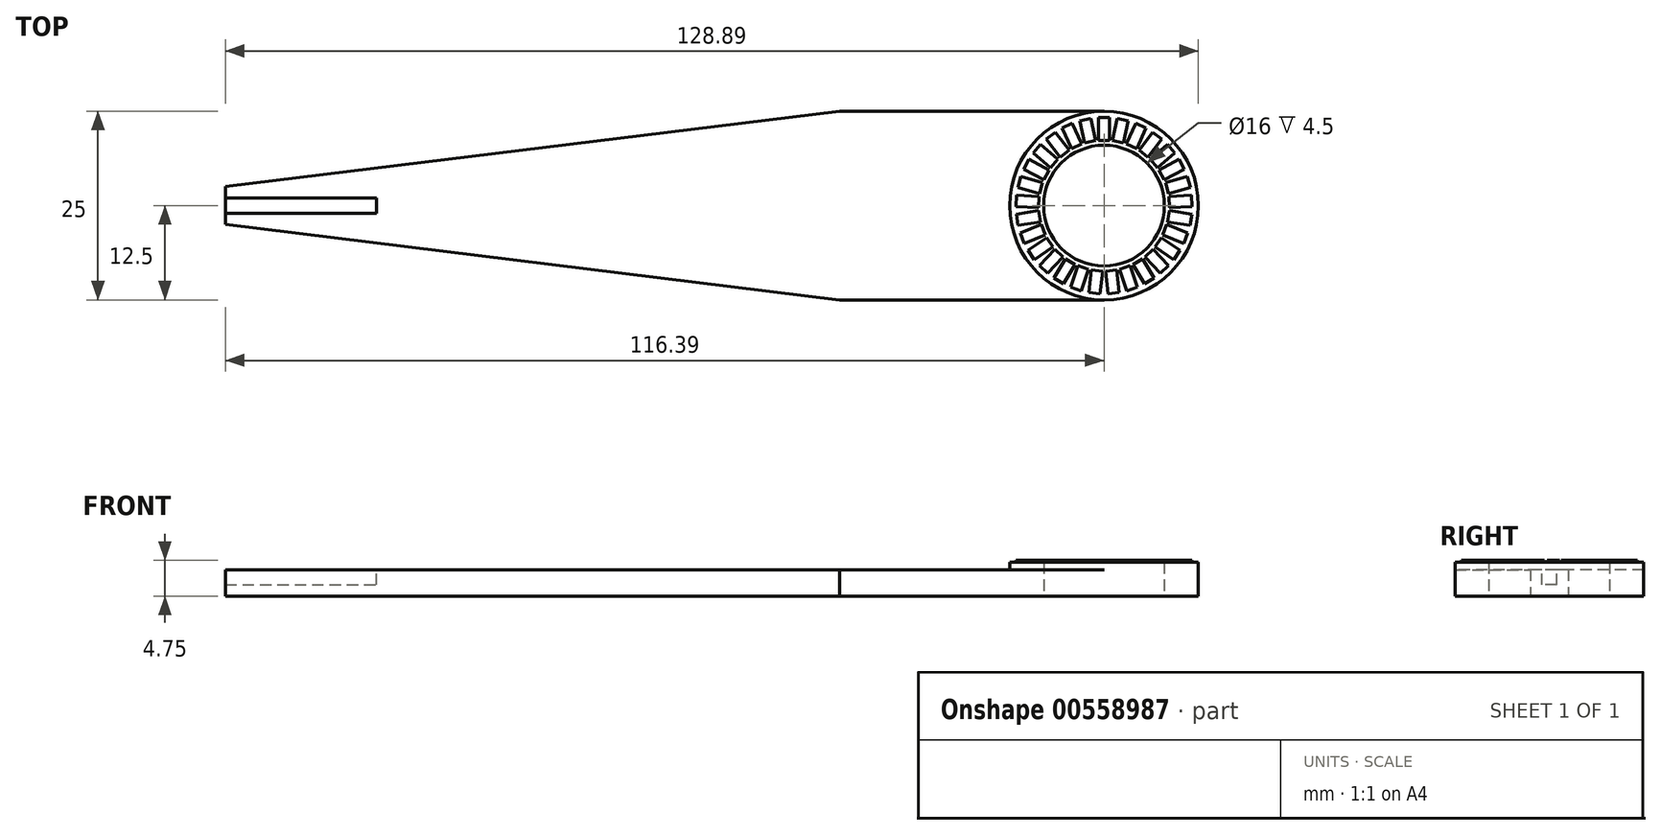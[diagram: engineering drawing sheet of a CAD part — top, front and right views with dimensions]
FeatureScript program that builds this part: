
annotation { "Feature Type Name" : "Feature", "Feature Type Description" : "" }
export const myFeature = defineFeature(function(context is Context, id is Id, definition is map)
    precondition{}
    {
        {
            var Q0;
            Q0=qCreatedBy(makeId("Top.planeOp"),FACE);
            var sketch = newSketch(context, id + "F0", { "sketchPlane" : qUnion([Q0])});
            skCircle(sketch, "E0", {"center": v(0, 0) * mm, "radius": 8 * mm});
            skCircle(sketch, "E1", {"center": v(0, 0) * mm, "radius": 12.5 * mm});
            skLineSegment(sketch, "E2", {"start": v(-35, 12.5) * mm, "end": v(0, 12.5) * mm});
            skLineSegment(sketch, "E3", {"start": v(-35, -12.5) * mm, "end": v(0, -12.5) * mm});
            skLineSegment(sketch, "E4", {"start": v(-35, 12.5) * mm, "end": v(-121.4, 12.5) * mm, "construction": true});
            skLineSegment(sketch, "E5", {"start": v(-35, 12.5) * mm, "end": v(-116.39, 2.5) * mm});
            skLineSegment(sketch, "E6", {"start": v(-35, -12.5) * mm, "end": v(-123.46, -12.5) * mm, "construction": true});
            skLineSegment(sketch, "E7", {"start": v(-35, -12.5) * mm, "end": v(-116.39, -2.5) * mm});
            skLineSegment(sketch, "E8", {"start": v(-116.39, 2.5) * mm, "end": v(-116.39, -2.5) * mm});
            skSolve(sketch);
        }
        {
            var Q0;
            Q0=qSketchRegion(id+"F0",true);
            extrude(context, id + "F1", {"entities" : qUnion([Q0]), "depth" : 3.5 * mm});
        }
        {
            var Q0;
            Q0=makeQuery(id+"F1.opExtrude","CAP_FACE",FACE,{"disambiguationData":[OSD([sQuery(id+"F0.wireOp",EDGE,"E0"),sQuery(id+"F0.wireOp",EDGE,"E1"),sQuery(id+"F0.wireOp",EDGE,"E2"),sQuery(id+"F0.wireOp",EDGE,"E3"),sQuery(id+"F0.wireOp",EDGE,"E5"),sQuery(id+"F0.wireOp",EDGE,"E7"),sQuery(id+"F0.wireOp",EDGE,"E8")])],"isStart":false});
            var sketch = newSketch(context, id + "F2", { "sketchPlane" : qUnion([Q0])});
            skCircle(sketch, "E9", {"center": v(0, 0) * mm, "radius": 12.5 * mm});
            skCircle(sketch, "E10", {"center": v(0, 0) * mm, "radius": 8 * mm});
            skSolve(sketch);
        }
        {
            var Q0;
            Q0=qSketchRegion(id+"F2",true);
            extrude(context, id + "F3", {"entities" : qUnion([Q0]), "operationType" : NewBodyOperationType.ADD, "depth" : 1 * mm});
        }
        {
            var Q0;
            Q0=makeQuery(id+"F1.opExtrude","CAP_FACE",FACE,{"disambiguationData":[OSD([sQuery(id+"F0.wireOp",EDGE,"E0"),sQuery(id+"F0.wireOp",EDGE,"E1"),sQuery(id+"F0.wireOp",EDGE,"E2"),sQuery(id+"F0.wireOp",EDGE,"E3"),sQuery(id+"F0.wireOp",EDGE,"E5"),sQuery(id+"F0.wireOp",EDGE,"E7"),sQuery(id+"F0.wireOp",EDGE,"E8")])],"isStart":false});
            var sketch = newSketch(context, id + "F4", { "sketchPlane" : qUnion([Q0])});
            skLineSegment(sketch, "E11.bottom", {"start": v(-116.39, 1) * mm, "end": v(-96.39, 1) * mm});
            skLineSegment(sketch, "E11.top", {"start": v(-116.39, -1) * mm, "end": v(-96.39, -1) * mm});
            skLineSegment(sketch, "E11.left", {"start": v(-116.39, 1) * mm, "end": v(-116.39, -1) * mm});
            skLineSegment(sketch, "E11.right", {"start": v(-96.39, 1) * mm, "end": v(-96.39, -1) * mm});
            skSolve(sketch);
        }
        {
            var Q0;
            Q0=qSketchRegion(id+"F4",true);
            extrude(context, id + "F5", {"entities" : qUnion([Q0]), "operationType" : NewBodyOperationType.REMOVE, "oppositeDirection" : true, "depth" : 2 * mm});
        }
        {
            var Q0;
            Q0=makeQuery(id+"F3.opExtrude","CAP_FACE",FACE,{"disambiguationData":[OSD([sQuery(id+"F2.wireOp",EDGE,"E9"),sQuery(id+"F2.wireOp",EDGE,"E10")])],"isStart":false});
            var sketch = newSketch(context, id + "F6", { "sketchPlane" : qUnion([Q0])});
            skLineSegment(sketch, "E12.bottom", {"start": v(-0.75, 11.65) * mm, "end": v(0.75, 11.65) * mm});
            skLineSegment(sketch, "E12.top", {"start": v(-0.75, 8.65) * mm, "end": v(0.75, 8.65) * mm});
            skLineSegment(sketch, "E12.left", {"start": v(-0.75, 11.65) * mm, "end": v(-0.75, 8.65) * mm});
            skLineSegment(sketch, "E12.right", {"start": v(0.75, 11.65) * mm, "end": v(0.75, 8.65) * mm});
            skLineSegment(sketch, "E13.1.0", {"start": v(1.77, 11.54) * mm, "end": v(1.13, 8.61) * mm});
            skLineSegment(sketch, "E13.1.1", {"start": v(1.13, 8.61) * mm, "end": v(2.6, 8.29) * mm});
            skLineSegment(sketch, "E13.1.2", {"start": v(1.77, 11.54) * mm, "end": v(3.24, 11.22) * mm});
            skLineSegment(sketch, "E13.1.3", {"start": v(3.24, 11.22) * mm, "end": v(2.6, 8.29) * mm});
            skLineSegment(sketch, "E13.2.0", {"start": v(4.21, 10.9) * mm, "end": v(2.95, 8.17) * mm});
            skLineSegment(sketch, "E13.2.1", {"start": v(2.95, 8.17) * mm, "end": v(4.31, 7.54) * mm});
            skLineSegment(sketch, "E13.2.2", {"start": v(4.21, 10.9) * mm, "end": v(5.57, 10.26) * mm});
            skLineSegment(sketch, "E13.2.3", {"start": v(5.57, 10.26) * mm, "end": v(4.31, 7.54) * mm});
            skLineSegment(sketch, "E13.3.0", {"start": v(6.46, 9.73) * mm, "end": v(4.64, 7.34) * mm});
            skLineSegment(sketch, "E13.3.1", {"start": v(4.64, 7.34) * mm, "end": v(5.83, 6.43) * mm});
            skLineSegment(sketch, "E13.3.2", {"start": v(6.46, 9.73) * mm, "end": v(7.65, 8.82) * mm});
            skLineSegment(sketch, "E13.3.3", {"start": v(7.65, 8.82) * mm, "end": v(5.83, 6.43) * mm});
            skLineSegment(sketch, "E13.4.0", {"start": v(8.4, 8.12) * mm, "end": v(6.1, 6.17) * mm});
            skLineSegment(sketch, "E13.4.1", {"start": v(6.1, 6.17) * mm, "end": v(7.08, 5.03) * mm});
            skLineSegment(sketch, "E13.4.2", {"start": v(8.4, 8.12) * mm, "end": v(9.37, 6.97) * mm});
            skLineSegment(sketch, "E13.4.3", {"start": v(9.37, 6.97) * mm, "end": v(7.08, 5.03) * mm});
            skLineSegment(sketch, "E13.5.0", {"start": v(9.94, 6.12) * mm, "end": v(7.3, 4.72) * mm});
            skLineSegment(sketch, "E13.5.1", {"start": v(7.3, 4.72) * mm, "end": v(8, 3.4) * mm});
            skLineSegment(sketch, "E13.5.2", {"start": v(9.94, 6.12) * mm, "end": v(10.65, 4.8) * mm});
            skLineSegment(sketch, "E13.5.3", {"start": v(10.65, 4.8) * mm, "end": v(8, 3.4) * mm});
            skLineSegment(sketch, "E13.6.0", {"start": v(11.03, 3.84) * mm, "end": v(8.14, 3.04) * mm});
            skLineSegment(sketch, "E13.6.1", {"start": v(8.14, 3.04) * mm, "end": v(8.54, 1.6) * mm});
            skLineSegment(sketch, "E13.6.2", {"start": v(11.03, 3.84) * mm, "end": v(11.43, 2.4) * mm});
            skLineSegment(sketch, "E13.6.3", {"start": v(11.43, 2.4) * mm, "end": v(8.54, 1.6) * mm});
            skLineSegment(sketch, "E13.7.0", {"start": v(11.6, 1.38) * mm, "end": v(8.6, 1.22) * mm});
            skLineSegment(sketch, "E13.7.1", {"start": v(8.6, 1.22) * mm, "end": v(8.68, -0.28) * mm});
            skLineSegment(sketch, "E13.7.2", {"start": v(11.6, 1.38) * mm, "end": v(11.68, -0.12) * mm});
            skLineSegment(sketch, "E13.7.3", {"start": v(11.68, -0.12) * mm, "end": v(8.68, -0.28) * mm});
            skLineSegment(sketch, "E13.8.0", {"start": v(11.62, -1.15) * mm, "end": v(8.66, -0.66) * mm});
            skLineSegment(sketch, "E13.8.1", {"start": v(8.66, -0.66) * mm, "end": v(8.42, -2.14) * mm});
            skLineSegment(sketch, "E13.8.2", {"start": v(11.62, -1.15) * mm, "end": v(11.38, -2.63) * mm});
            skLineSegment(sketch, "E13.8.3", {"start": v(11.38, -2.63) * mm, "end": v(8.42, -2.14) * mm});
            skLineSegment(sketch, "E13.9.0", {"start": v(11.1, -3.62) * mm, "end": v(8.32, -2.5) * mm});
            skLineSegment(sketch, "E13.9.1", {"start": v(8.32, -2.5) * mm, "end": v(7.76, -3.9) * mm});
            skLineSegment(sketch, "E13.9.2", {"start": v(11.1, -3.62) * mm, "end": v(10.55, -5.01) * mm});
            skLineSegment(sketch, "E13.9.3", {"start": v(10.55, -5.01) * mm, "end": v(7.76, -3.9) * mm});
            skLineSegment(sketch, "E13.10.0", {"start": v(10.07, -5.92) * mm, "end": v(7.58, -4.24) * mm});
            skLineSegment(sketch, "E13.10.1", {"start": v(7.58, -4.24) * mm, "end": v(6.74, -5.48) * mm});
            skLineSegment(sketch, "E13.10.2", {"start": v(10.07, -5.92) * mm, "end": v(9.22, -7.16) * mm});
            skLineSegment(sketch, "E13.10.3", {"start": v(9.22, -7.16) * mm, "end": v(6.74, -5.48) * mm});
            skLineSegment(sketch, "E13.11.0", {"start": v(8.56, -7.94) * mm, "end": v(6.5, -5.77) * mm});
            skLineSegment(sketch, "E13.11.1", {"start": v(6.5, -5.77) * mm, "end": v(5.4, -6.8) * mm});
            skLineSegment(sketch, "E13.11.2", {"start": v(8.56, -7.94) * mm, "end": v(7.47, -8.98) * mm});
            skLineSegment(sketch, "E13.11.3", {"start": v(7.47, -8.98) * mm, "end": v(5.4, -6.8) * mm});
            skLineSegment(sketch, "E13.12.0", {"start": v(6.65, -9.6) * mm, "end": v(5.1, -7.03) * mm});
            skLineSegment(sketch, "E13.12.1", {"start": v(5.1, -7.03) * mm, "end": v(3.82, -7.8) * mm});
            skLineSegment(sketch, "E13.12.2", {"start": v(6.65, -9.6) * mm, "end": v(5.37, -10.37) * mm});
            skLineSegment(sketch, "E13.12.3", {"start": v(5.37, -10.37) * mm, "end": v(3.82, -7.8) * mm});
            skLineSegment(sketch, "E13.13.0", {"start": v(4.43, -10.8) * mm, "end": v(3.47, -7.96) * mm});
            skLineSegment(sketch, "E13.13.1", {"start": v(3.47, -7.96) * mm, "end": v(2.05, -8.44) * mm});
            skLineSegment(sketch, "E13.13.2", {"start": v(4.43, -10.8) * mm, "end": v(3.01, -11.28) * mm});
            skLineSegment(sketch, "E13.13.3", {"start": v(3.01, -11.28) * mm, "end": v(2.05, -8.44) * mm});
            skLineSegment(sketch, "E13.14.0", {"start": v(2, -11.5) * mm, "end": v(1.68, -8.52) * mm});
            skLineSegment(sketch, "E13.14.1", {"start": v(1.68, -8.52) * mm, "end": v(0.19, -8.68) * mm});
            skLineSegment(sketch, "E13.14.2", {"start": v(2, -11.5) * mm, "end": v(0.51, -11.67) * mm});
            skLineSegment(sketch, "E13.14.3", {"start": v(0.51, -11.67) * mm, "end": v(0.19, -8.68) * mm});
            skLineSegment(sketch, "E13.15.0", {"start": v(-0.51, -11.67) * mm, "end": v(-0.19, -8.68) * mm});
            skLineSegment(sketch, "E13.15.1", {"start": v(-0.19, -8.68) * mm, "end": v(-1.68, -8.52) * mm});
            skLineSegment(sketch, "E13.15.2", {"start": v(-0.51, -11.67) * mm, "end": v(-2, -11.5) * mm});
            skLineSegment(sketch, "E13.15.3", {"start": v(-2, -11.5) * mm, "end": v(-1.68, -8.52) * mm});
            skLineSegment(sketch, "E13.16.0", {"start": v(-3.01, -11.28) * mm, "end": v(-2.05, -8.44) * mm});
            skLineSegment(sketch, "E13.16.1", {"start": v(-2.05, -8.44) * mm, "end": v(-3.47, -7.96) * mm});
            skLineSegment(sketch, "E13.16.2", {"start": v(-3.01, -11.28) * mm, "end": v(-4.43, -10.8) * mm});
            skLineSegment(sketch, "E13.16.3", {"start": v(-4.43, -10.8) * mm, "end": v(-3.47, -7.96) * mm});
            skLineSegment(sketch, "E13.17.0", {"start": v(-5.37, -10.37) * mm, "end": v(-3.82, -7.8) * mm});
            skLineSegment(sketch, "E13.17.1", {"start": v(-3.82, -7.8) * mm, "end": v(-5.1, -7.03) * mm});
            skLineSegment(sketch, "E13.17.2", {"start": v(-5.37, -10.37) * mm, "end": v(-6.65, -9.6) * mm});
            skLineSegment(sketch, "E13.17.3", {"start": v(-6.65, -9.6) * mm, "end": v(-5.1, -7.03) * mm});
            skLineSegment(sketch, "E13.18.0", {"start": v(-7.47, -8.98) * mm, "end": v(-5.4, -6.8) * mm});
            skLineSegment(sketch, "E13.18.1", {"start": v(-5.4, -6.8) * mm, "end": v(-6.5, -5.77) * mm});
            skLineSegment(sketch, "E13.18.2", {"start": v(-7.47, -8.98) * mm, "end": v(-8.56, -7.94) * mm});
            skLineSegment(sketch, "E13.18.3", {"start": v(-8.56, -7.94) * mm, "end": v(-6.5, -5.77) * mm});
            skLineSegment(sketch, "E13.19.0", {"start": v(-9.22, -7.16) * mm, "end": v(-6.74, -5.48) * mm});
            skLineSegment(sketch, "E13.19.1", {"start": v(-6.74, -5.48) * mm, "end": v(-7.58, -4.24) * mm});
            skLineSegment(sketch, "E13.19.2", {"start": v(-9.22, -7.16) * mm, "end": v(-10.07, -5.92) * mm});
            skLineSegment(sketch, "E13.19.3", {"start": v(-10.07, -5.92) * mm, "end": v(-7.58, -4.24) * mm});
            skLineSegment(sketch, "E13.20.0", {"start": v(-10.55, -5.01) * mm, "end": v(-7.76, -3.9) * mm});
            skLineSegment(sketch, "E13.20.1", {"start": v(-7.76, -3.9) * mm, "end": v(-8.32, -2.5) * mm});
            skLineSegment(sketch, "E13.20.2", {"start": v(-10.55, -5.01) * mm, "end": v(-11.1, -3.62) * mm});
            skLineSegment(sketch, "E13.20.3", {"start": v(-11.1, -3.62) * mm, "end": v(-8.32, -2.5) * mm});
            skLineSegment(sketch, "E13.21.0", {"start": v(-11.38, -2.63) * mm, "end": v(-8.42, -2.14) * mm});
            skLineSegment(sketch, "E13.21.1", {"start": v(-8.42, -2.14) * mm, "end": v(-8.66, -0.66) * mm});
            skLineSegment(sketch, "E13.21.2", {"start": v(-11.38, -2.63) * mm, "end": v(-11.62, -1.15) * mm});
            skLineSegment(sketch, "E13.21.3", {"start": v(-11.62, -1.15) * mm, "end": v(-8.66, -0.66) * mm});
            skLineSegment(sketch, "E13.22.0", {"start": v(-11.68, -0.12) * mm, "end": v(-8.68, -0.28) * mm});
            skLineSegment(sketch, "E13.22.1", {"start": v(-8.68, -0.28) * mm, "end": v(-8.6, 1.22) * mm});
            skLineSegment(sketch, "E13.22.2", {"start": v(-11.68, -0.12) * mm, "end": v(-11.6, 1.38) * mm});
            skLineSegment(sketch, "E13.22.3", {"start": v(-11.6, 1.38) * mm, "end": v(-8.6, 1.22) * mm});
            skLineSegment(sketch, "E13.23.0", {"start": v(-11.43, 2.4) * mm, "end": v(-8.54, 1.6) * mm});
            skLineSegment(sketch, "E13.23.1", {"start": v(-8.54, 1.6) * mm, "end": v(-8.14, 3.04) * mm});
            skLineSegment(sketch, "E13.23.2", {"start": v(-11.43, 2.4) * mm, "end": v(-11.03, 3.84) * mm});
            skLineSegment(sketch, "E13.23.3", {"start": v(-11.03, 3.84) * mm, "end": v(-8.14, 3.04) * mm});
            skLineSegment(sketch, "E13.24.0", {"start": v(-10.65, 4.8) * mm, "end": v(-8, 3.4) * mm});
            skLineSegment(sketch, "E13.24.1", {"start": v(-8, 3.4) * mm, "end": v(-7.3, 4.72) * mm});
            skLineSegment(sketch, "E13.24.2", {"start": v(-10.65, 4.8) * mm, "end": v(-9.94, 6.12) * mm});
            skLineSegment(sketch, "E13.24.3", {"start": v(-9.94, 6.12) * mm, "end": v(-7.3, 4.72) * mm});
            skLineSegment(sketch, "E13.25.0", {"start": v(-9.37, 6.97) * mm, "end": v(-7.08, 5.03) * mm});
            skLineSegment(sketch, "E13.25.1", {"start": v(-7.08, 5.03) * mm, "end": v(-6.1, 6.17) * mm});
            skLineSegment(sketch, "E13.25.2", {"start": v(-9.37, 6.97) * mm, "end": v(-8.4, 8.12) * mm});
            skLineSegment(sketch, "E13.25.3", {"start": v(-8.4, 8.12) * mm, "end": v(-6.1, 6.17) * mm});
            skLineSegment(sketch, "E13.26.0", {"start": v(-7.65, 8.82) * mm, "end": v(-5.83, 6.43) * mm});
            skLineSegment(sketch, "E13.26.1", {"start": v(-5.83, 6.43) * mm, "end": v(-4.64, 7.34) * mm});
            skLineSegment(sketch, "E13.26.2", {"start": v(-7.65, 8.82) * mm, "end": v(-6.46, 9.73) * mm});
            skLineSegment(sketch, "E13.26.3", {"start": v(-6.46, 9.73) * mm, "end": v(-4.64, 7.34) * mm});
            skLineSegment(sketch, "E13.27.0", {"start": v(-5.57, 10.26) * mm, "end": v(-4.31, 7.54) * mm});
            skLineSegment(sketch, "E13.27.1", {"start": v(-4.31, 7.54) * mm, "end": v(-2.95, 8.17) * mm});
            skLineSegment(sketch, "E13.27.2", {"start": v(-5.57, 10.26) * mm, "end": v(-4.21, 10.9) * mm});
            skLineSegment(sketch, "E13.27.3", {"start": v(-4.21, 10.9) * mm, "end": v(-2.95, 8.17) * mm});
            skLineSegment(sketch, "E13.28.0", {"start": v(-3.24, 11.22) * mm, "end": v(-2.6, 8.29) * mm});
            skLineSegment(sketch, "E13.28.1", {"start": v(-2.6, 8.29) * mm, "end": v(-1.13, 8.61) * mm});
            skLineSegment(sketch, "E13.28.2", {"start": v(-3.24, 11.22) * mm, "end": v(-1.77, 11.54) * mm});
            skLineSegment(sketch, "E13.28.3", {"start": v(-1.77, 11.54) * mm, "end": v(-1.13, 8.61) * mm});
            skPoint(sketch, "E13.center", {"position": v(0, 0) * mm});
            skLineSegment(sketch, "E13.anchor1", {"start": v(0, 0) * mm, "end": v(-0.75, 8.65) * mm, "construction": true});
            skLineSegment(sketch, "E13.anchor2", {"start": v(0, 0) * mm, "end": v(-0.75, 8.65) * mm, "construction": true});
            skSolve(sketch);
        }
        {
            var Q0;
            Q0=qSketchRegion(id+"F6",true);
            extrude(context, id + "F7", {"entities" : qUnion([Q0]), "operationType" : NewBodyOperationType.ADD, "depth" : .25 * mm});
        }
    });
